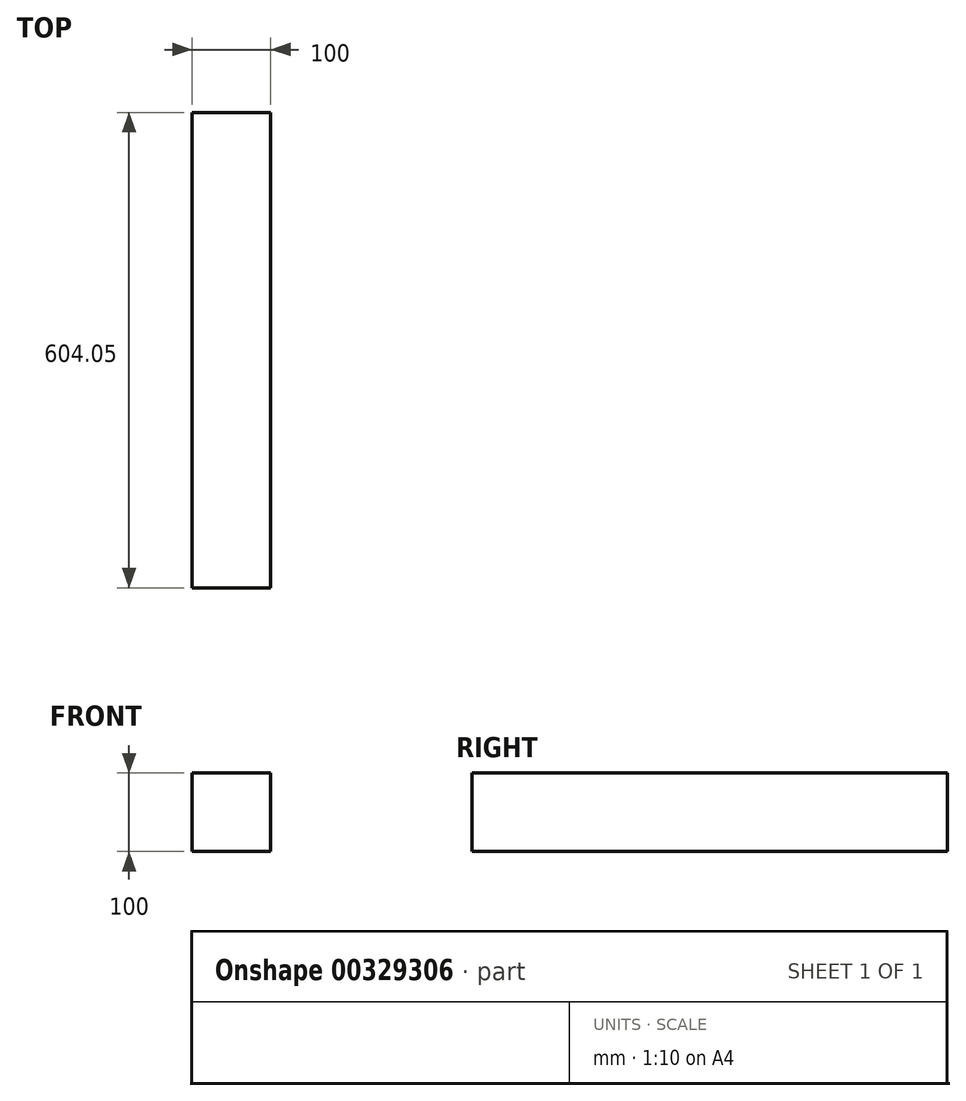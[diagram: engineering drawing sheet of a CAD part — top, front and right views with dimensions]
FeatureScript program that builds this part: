
annotation { "Feature Type Name" : "Feature", "Feature Type Description" : "" }
export const myFeature = defineFeature(function(context is Context, id is Id, definition is map)
    precondition{}
    {
        {
            var Q0;
            Q0=qCreatedBy(makeId("Front.planeOp"),FACE);
            var sketch = newSketch(context, id + "F0", { "sketchPlane" : qUnion([Q0])});
            skLineSegment(sketch, "E0.bottom", {"start": v(0, 0) * mm, "end": v(-100, 0) * mm, "construction": true});
            skLineSegment(sketch, "E0.top", {"start": v(0, 100) * mm, "end": v(-100, 100) * mm, "construction": true});
            skLineSegment(sketch, "E0.left", {"start": v(0, 0) * mm, "end": v(0, 100) * mm, "construction": true});
            skLineSegment(sketch, "E0.right", {"start": v(-100, 0) * mm, "end": v(-100, 100) * mm, "construction": true});
            skLineSegment(sketch, "E1.bottom", {"start": v(-100, 100) * mm, "end": v(0, 100) * mm});
            skLineSegment(sketch, "E1.top", {"start": v(-100, 0) * mm, "end": v(0, 0) * mm});
            skLineSegment(sketch, "E1.left", {"start": v(-100, 100) * mm, "end": v(-100, 0) * mm});
            skLineSegment(sketch, "E1.right", {"start": v(0, 100) * mm, "end": v(0, 0) * mm});
            skSolve(sketch);
        }
        {
            var Q0;
            Q0=makeQuery(id+"F0.imprint","IMPRINT",FACE,{"disambiguationData":[TD([[makeQuery(id+"F0.imprint","IMPRINT",EDGE,{"derivedFrom":sQuery(id+"F0.wireOp",EDGE,"E1.bottom")}),-1.0]])]});
            extrude(context, id + "F1", {"entities" : qUnion([Q0]), "depth" : 604.05 * mm});
        }
    });
